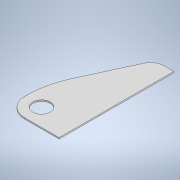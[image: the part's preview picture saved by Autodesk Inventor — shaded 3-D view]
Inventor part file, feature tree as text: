
AUTODESK INVENTOR PART (.ipt)
format: ipt  version: 2022 (Build 260153000, 153)  size: 122,368 bytes
history: native  units: mm
features: fillet x3, other x2, sketch x1
ambient origin geometry x8: Origin, YZ Plane, XZ Plane, XY Plane, X Axis, Y Axis, Z Axis, Center Point
bodies: Solid1 (feature_tree)
feature tree (6):
  other  "Beslag_stempel"
  fillet  "Fillet1"  Radius=45.0mm
  fillet  "Fillet2"  Radius=40.0mm
  fillet  "Fillet3"  Radius=20.0mm
  sketch  "Sketch1"  dims[d3=20.0mm d4=130.0mm d5=20.0mm d6=1.5mm d7=20.5mm d8=103.25mm d9=15.5mm]
  other  "Plate1"
